# Revit family: LSS26333A75FTB-T.V3,A2FTB-T.V3
name_source: partatom
category: Plumbing Fixtures
revit_build: Autodesk Revit LT 2017 (Build: 20160225_1515(x64)
units: mm (PartAtom-declared; Revit-internal decimal feet)

## family parameters
Always vertical = Yes
Cut with Voids When Loaded = No
OmniClass Number = 23.45.05.14.17
OmniClass Title = Showers
Part Type = Normal
Room Calculation Point = No
Round Connector Dimension = Use Diameter
Shared = No
Work Plane-Based = No

## types (2) — shared parameters
Assembly Code = D2010710
Description = Trench Drain, 12 x 18 Subway Tile, Transfer Threshold
Keynote = 22 40 00.B3
Manufacturer = best bath
Model = LBS26333A75FTT.V3
Threshold Height = 3/4"
Type Comments = ADA Compliant
URL = http://www.bestbath.com
Unit Depth = 34"
Unit Height = 78 3/4"
Unit Width = 63"

## type names (no varying parameters)
- LBS26333A75FTB.V3
- LBS26333A75FTT.V3

## geometry (parser evidence)
native form markers: Blend x16, Sweep x6
no freeform markers — native parametric forms only
